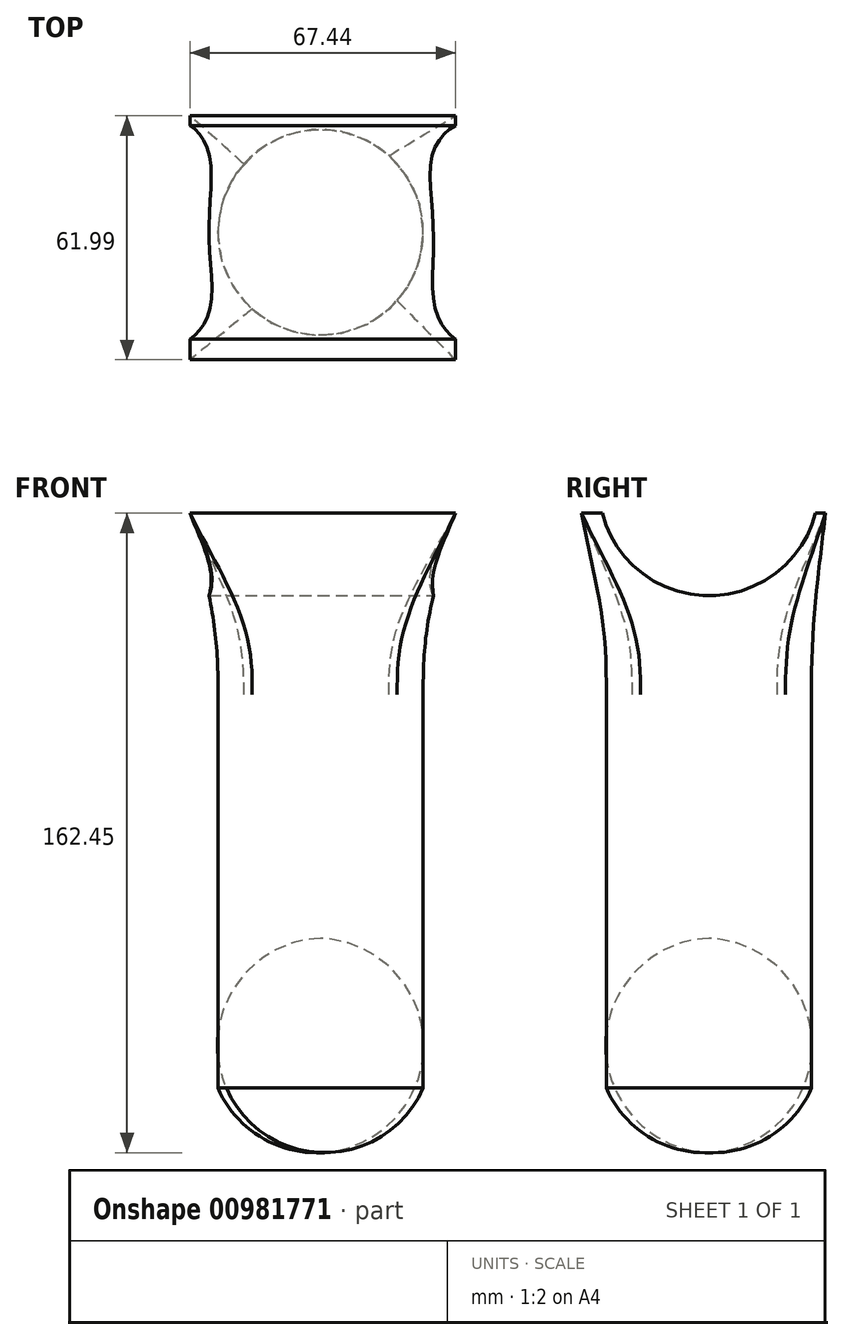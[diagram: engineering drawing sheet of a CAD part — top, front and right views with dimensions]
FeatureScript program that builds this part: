
annotation { "Feature Type Name" : "Feature", "Feature Type Description" : "" }
export const myFeature = defineFeature(function(context is Context, id is Id, definition is map)
    precondition{}
    {
        {
            var Q0;
            Q0=qCreatedBy(makeId("Front.planeOp"),FACE);
            var sketch = newSketch(context, id + "F0", { "sketchPlane" : qUnion([Q0])});
            skLineSegment(sketch, "E0", {"start": v(-111.66, 33.96) * mm, "end": v(-85.6, 33.96) * mm});
            skLineSegment(sketch, "E1", {"start": v(-85.6, 33.96) * mm, "end": v(-85.6, 17.57) * mm});
            skArc(sketch, "E2", {"start": v(-111.66, 33.96) * mm, "mid": v(-101.16, 21.73) * mm, "end": v(-85.6, 17.57) * mm});
            skSolve(sketch);
        }
        {
            var Q0;
            Q0=makeQuery(id+"F0.imprint","IMPRINT",FACE,{"disambiguationData":[TD([[makeQuery(id+"F0.imprint","IMPRINT",EDGE,{"derivedFrom":sQuery(id+"F0.wireOp",EDGE,"E0")}),-1.0]])]});
            var Q1;
            Q1=sQuery(id+"F0.wireOp",EDGE,"E1");
            revolve(context, id + "F1", {"surfaceOperationType" : NewSurfaceOperationType.NEW, "entities" : qUnion([Q0]), "axis" : qUnion([Q1]), "revolveType" : RevolveType.FULL});
        }
        {
            var Q0;
            Q0=makeQuery(id+"F1.opRevolve","SWEPT_FACE",FACE,{"disambiguationData":[OSD([sQuery(id+"F0.wireOp",EDGE,"E0")])]});
            extrude(context, id + "F2", {"entities" : qUnion([Q0]), "operationType" : NewBodyOperationType.ADD, "depth" : 100 * mm, "offsetDistance" : 25 * mm});
        }
        {
            var Q0;
            Q0=qCreatedBy(makeId("Top.planeOp"),FACE);
            cPlane(context, id + "F3", {"entities" : qUnion([Q0]), "cplaneType" : CPlaneType.OFFSET, "offset" : 180 * mm, "width" : 150 * mm, "height" : 150 * mm});
        }
        {
            var Q0;
            Q0=qCreatedBy(id+"F3.planeOp",FACE);
            var sketch = newSketch(context, id + "F4", { "sketchPlane" : qUnion([Q0])});
            skLineSegment(sketch, "E3.bottom", {"start": v(-118.76, 29.59) * mm, "end": v(-51.32, 29.59) * mm});
            skLineSegment(sketch, "E3.top", {"start": v(-118.76, -32.4) * mm, "end": v(-51.32, -32.4) * mm});
            skLineSegment(sketch, "E3.left", {"start": v(-118.76, 29.59) * mm, "end": v(-118.76, -32.4) * mm});
            skLineSegment(sketch, "E3.right", {"start": v(-51.32, 29.59) * mm, "end": v(-51.32, -32.4) * mm});
            skSolve(sketch);
        }
        {
            var Q1;
            Q1=makeQuery(id+"F2.opExtrude","CAP_FACE",FACE,{"disambiguationData":[OSD([sQuery(id+"F0.wireOp",EDGE,"E0")])],"isStart":false});
            var Q2;
            Q2=makeQuery(id+"F4.imprint","IMPRINT",FACE,{"disambiguationData":[TD([[makeQuery(id+"F4.imprint","IMPRINT",EDGE,{"derivedFrom":sQuery(id+"F4.wireOp",EDGE,"E3.bottom")}),-1.0]])]});
            loft(context, id + "F5", {"operationType" : NewBodyOperationType.ADD, "startCondition" : LoftEndDerivativeType.MATCH_CURVATURE, "startMagnitude" : 1, "sheetProfilesArray" : [{ "sheetProfileEntities" : qUnion([Q1]) }, { "sheetProfileEntities" : qUnion([Q2]) }]});
        }
        {
            var Q0;
            Q0=qCreatedBy(makeId("Right.planeOp"),FACE);
            var sketch = newSketch(context, id + "F6", { "sketchPlane" : qUnion([Q0])});
            skCircle(sketch, "E4", {"center": v(0, 187.06) * mm, "radius": 28 * mm});
            skSolve(sketch);
        }
        {
            var Q0;
            Q0=makeQuery(id+"F6.imprint","IMPRINT",FACE,{"disambiguationData":[TD([[makeQuery(id+"F6.imprint","IMPRINT",EDGE,{"derivedFrom":sQuery(id+"F6.wireOp",EDGE,"E4")}),1.0]])]});
            extrude(context, id + "F7", {"entities" : qUnion([Q0]), "operationType" : NewBodyOperationType.REMOVE, "oppositeDirection" : true, "depth" : 200 * mm, "offsetDistance" : 25 * mm});
        }
    });
